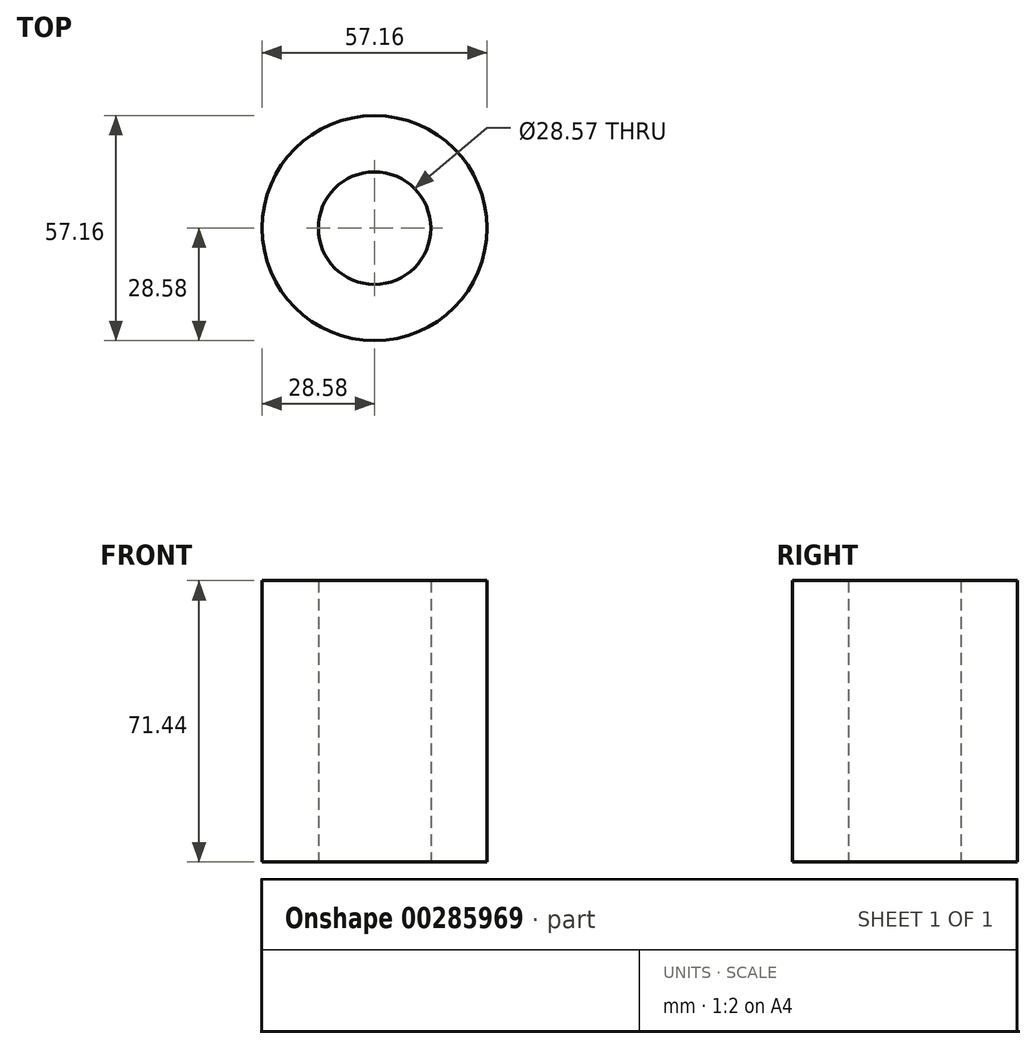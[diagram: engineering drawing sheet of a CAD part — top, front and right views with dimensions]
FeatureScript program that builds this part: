
annotation { "Feature Type Name" : "Feature", "Feature Type Description" : "" }
export const myFeature = defineFeature(function(context is Context, id is Id, definition is map)
    precondition{}
    {
        {
            var Q0;
            Q0=qCreatedBy(makeId("Top.planeOp"),FACE);
            var sketch = newSketch(context, id + "F0", { "sketchPlane" : qUnion([Q0])});
            skCircle(sketch, "E0", {"center": v(0, 0) * mm, "radius": 28.57 * mm});
            skCircle(sketch, "E1", {"center": v(0, 0) * mm, "radius": 14.29 * mm});
            skSolve(sketch);
        }
        {
            var Q0;
            Q0 = qSketchRegion(id + "F0", true);
            extrude(context, id + "F1", {"entities" : qUnion([Q0]), "depth" : 71.44 * mm});
        }
    });
